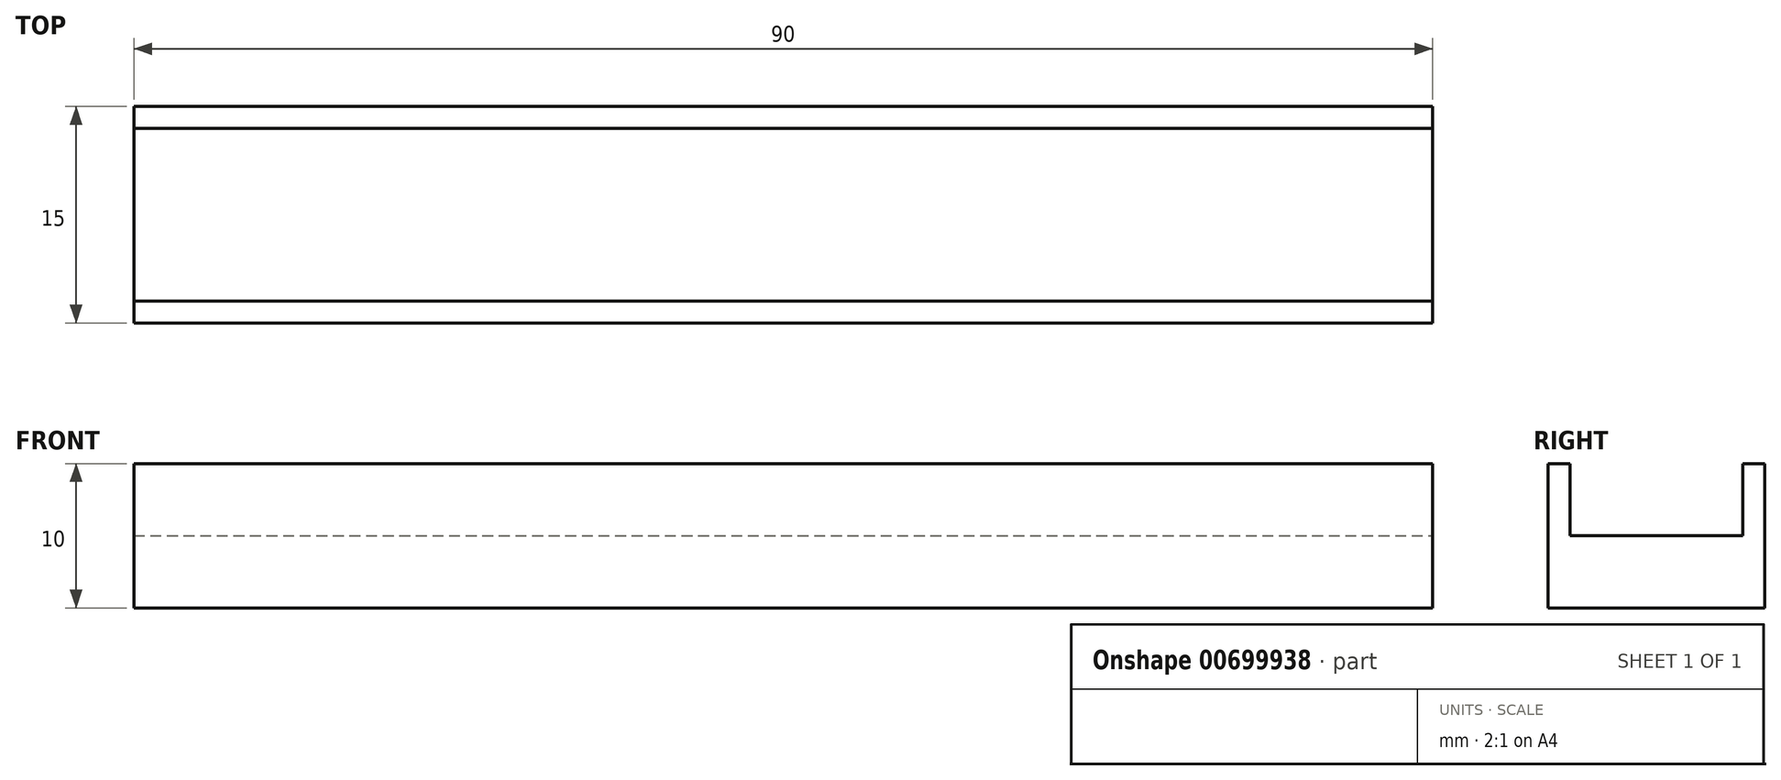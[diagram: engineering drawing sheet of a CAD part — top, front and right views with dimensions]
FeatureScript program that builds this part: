
annotation { "Feature Type Name" : "Feature", "Feature Type Description" : "" }
export const myFeature = defineFeature(function(context is Context, id is Id, definition is map)
    precondition{}
    {
        {
            var Q0;
            Q0=qCreatedBy(makeId("Top.planeOp"),FACE);
            var sketch = newSketch(context, id + "F0", { "sketchPlane" : qUnion([Q0])});
            skLineSegment(sketch, "E0.bottom", {"start": v(45, -7.5) * mm, "end": v(-45, -7.5) * mm});
            skLineSegment(sketch, "E0.top", {"start": v(45, 7.5) * mm, "end": v(-45, 7.5) * mm});
            skLineSegment(sketch, "E0.left", {"start": v(45, -7.5) * mm, "end": v(45, 7.5) * mm});
            skLineSegment(sketch, "E0.right", {"start": v(-45, -7.5) * mm, "end": v(-45, 7.5) * mm});
            skPoint(sketch, "E0.middle", {"position": v(0, 0) * mm});
            skSolve(sketch);
        }
        {
            var Q0;
            Q0=makeQuery(id+"F0.imprint","IMPRINT",FACE,{"disambiguationData":[TD([[makeQuery(id+"F0.imprint","IMPRINT",EDGE,{"derivedFrom":sQuery(id+"F0.wireOp",EDGE,"E0.bottom")}),-1.0]])]});
            extrude(context, id + "F1", {"entities" : qUnion([Q0]), "endBound" : BoundingType.SYMMETRIC, "depth" : 10 * mm, "offsetDistance" : 25 * mm});
        }
        {
            var Q0;
            Q0=makeQuery(id+"F1.opExtrude","CAP_FACE",FACE,{"disambiguationData":[OSD([sQuery(id+"F0.wireOp",EDGE,"E0.bottom"),sQuery(id+"F0.wireOp",EDGE,"E0.top"),sQuery(id+"F0.wireOp",EDGE,"E0.left"),sQuery(id+"F0.wireOp",EDGE,"E0.right")])],"isStart":false});
            var sketch = newSketch(context, id + "F2", { "sketchPlane" : qUnion([Q0])});
            skLineSegment(sketch, "E1", {"start": v(-45, 6) * mm, "end": v(45, 6) * mm});
            skLineSegment(sketch, "E2", {"start": v(45, -6) * mm, "end": v(-45, -6) * mm});
            skSolve(sketch);
        }
        {
            var Q0;
            {var subQ0=sQuery(id+"F2.wireOp",EDGE,"E1");Q0=makeQuery(id+"F2.imprint","IMPRINT",FACE,{"disambiguationData":[TD([[makeQuery(id+"F2.imprint","IMPRINT",EDGE,{"derivedFrom":subQ0}),-1.0]])]});}
            extrude(context, id + "F3", {"entities" : qUnion([Q0]), "operationType" : NewBodyOperationType.REMOVE, "oppositeDirection" : true, "depth" : 5 * mm, "offsetDistance" : 25 * mm});
        }
    });
